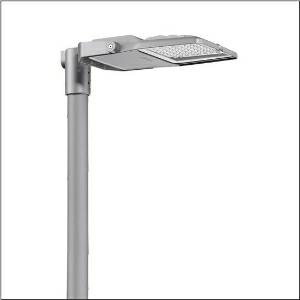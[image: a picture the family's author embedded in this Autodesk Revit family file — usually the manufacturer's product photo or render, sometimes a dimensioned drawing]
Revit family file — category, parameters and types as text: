
# Revit family: floodlight_fl_21_iq_mini___pl64_5xa7772d4e3a_9d14
name_source: partatom
category: Lighting Fixtures
units: mm (PartAtom-declared; Revit-internal decimal feet)

## family parameters
Cut with Voids When Loaded = No
Host = Face
Light Source = No
Part Type = Normal
Room Calculation Point = No
Round Connector Dimension = Use Diameter
Shared = No

## types (1)
- --- (1 x LED, 17970 lm, 143 W, 4000K)
    Apparent Load = 143 VA
    CIE Flux Codes = 28 80 98 100 100
    Color Rendering = 70
    Color Temperature = 4000K
    Default Elevation = 1800 mm
    Description = Floodlight FL 21 iQ mini, floodlight, primary light control with lens, of PMMA, primary optical cover: protective disc, of toughened safety glass, transparent, light distribution: PL64, light emission: direct distribution, installation type: surface-mounted, LED, High Power LED, rated luminous flux: 17.970lm, luminous efficacy: 126lm/W, light colour: 740, colour temperature: 4000K, control gear: iQ Street-Remote/DALI, control: Auto-Match, Temp-Guard, Night-Set, Smart-Wire, Desk-Remote (wireless, voltage-free reading and setting of iQ features in the workshop via application-optimized NFC function/RFID function), optimised constant luminous flux control (CLO 2.0), Light-Fading, Lumen-Switch, with terminal, 6-pole, mains connection: 220..240V, AC, 50/60Hz, start of lifetime: 143W, end of service life: 152W, reduction: 61W, luminaire housing, of diecast aluminium, powder-coated, Siteco® metallic grey (DB 702S), corrosivity category C5 mid according to DIN EN ISO 12944, suitable for swimming pools, chlorine-resistant, sealing non-destructively replaceable, please order mast flange separately, mast bracket, of steel, galvanised, powder-coated, protection rating (complete): IP66, insulation class (complete): insulation class II (safety insulation), certification: CE, ENEC, VDE, protection symbol: D, impact resistance: IK08, permissible operating ambient temperature: -40..+40°C, permissible operating ambient temperature for outdoor applications: -40..+50°C, standard: DIN EN 12944, LABS conformity tested according to VDMA 24364:2018-05, packaging unit: 1 piece

Light Distribution: PL64
    Height = 70 mm
    Lamp = 1 x LED
    Lamp Light Flux = 17970 lm
    Lamp Power = 143 W
    Lamp count = 1
    Length = 485 mm
    Luminous efficacy = 126 lm/W
    Manufacturer = Siteco
    ModVariant = No
    Model = 5XA7772D4E3A
    Number of Poles = 1
    OnlyDefault = Yes
    Power Factor = 1
    Product Name = Floodlight FL 21 iQ mini | PL64
    Product group = floodlight | pylon annexe
    ProductGroupID = 6201
    Protection Class = Protection class II
    Protection Degree = IP 66
    RLX_Detail_Level = 1
    RLX_Emergency_Light_Flux = 0 lm
    RLX_Emergency_Type = 0
    RLX_Emergency_Type_DB = No
    RlxData = <blob elided: 101613 chars, md5=4dbfb066>
    Socket = socket
    Standby Power = 0 W
    System Light Flux = 17970 lm
    System Power = 143 W
    Type Comments = factory setting: luminous flux: 100 % | dim-lin: 254 | 730 mA
    Type Image = l_1007125.jpg
    URL = http://relux.com
    VarID = @adj_187115
    Voltage = 0 V
    Weight = 0.00 kg
    Width = 337 mm

## geometry (parser evidence)
native form markers: Blend x4, Sweep x13
no freeform markers — native parametric forms only
